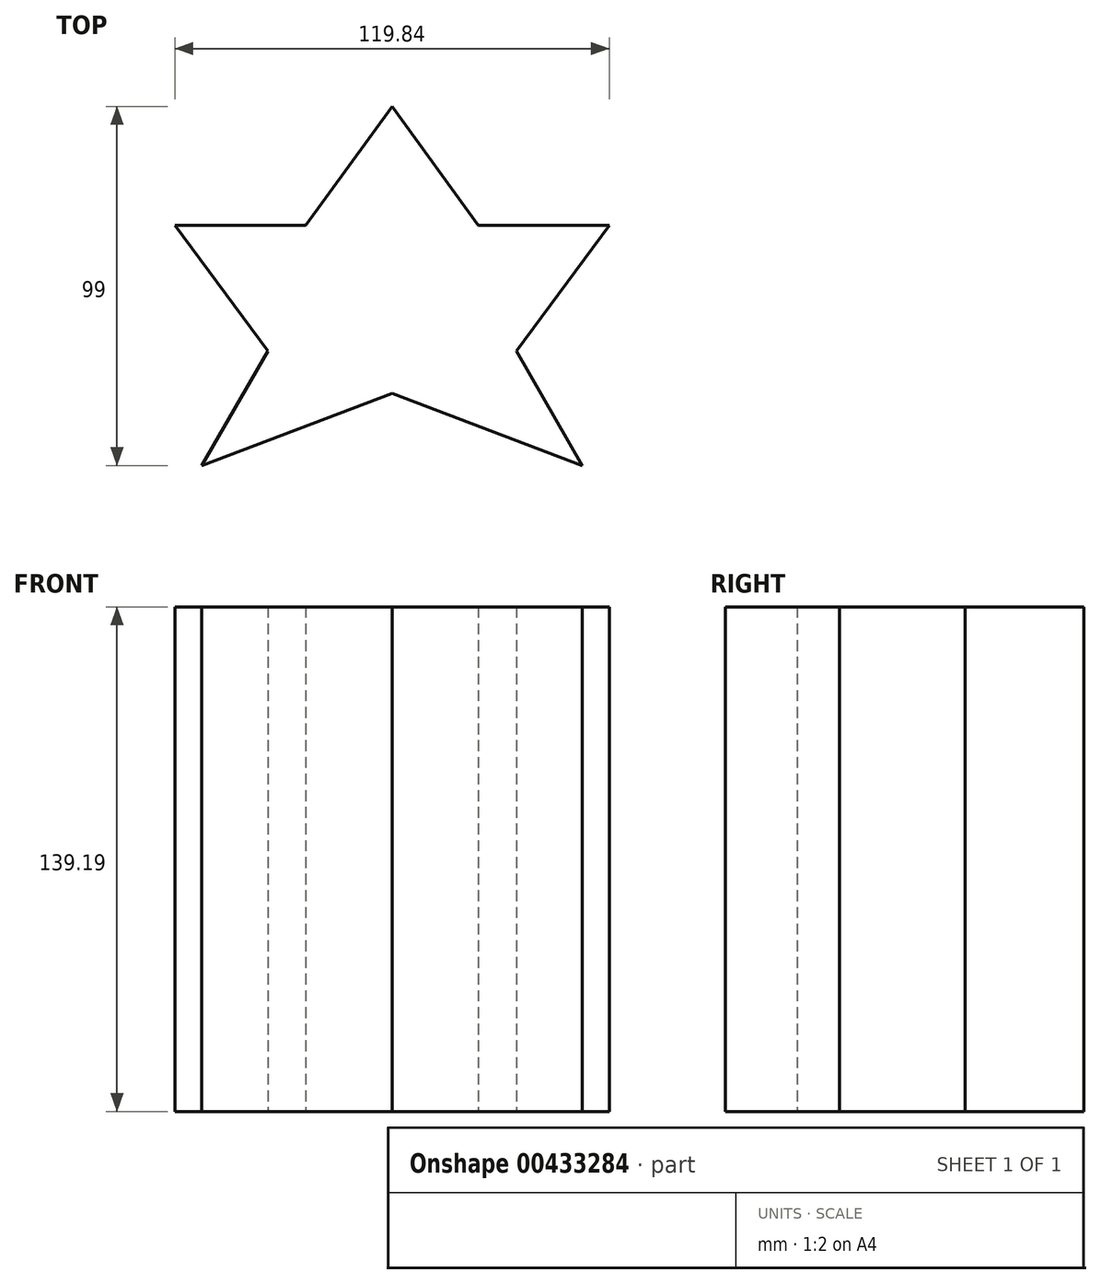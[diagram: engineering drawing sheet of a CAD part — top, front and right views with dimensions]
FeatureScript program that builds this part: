
annotation { "Feature Type Name" : "Feature", "Feature Type Description" : "" }
export const myFeature = defineFeature(function(context is Context, id is Id, definition is map)
    precondition{}
    {
        {
            var Q0;
            Q0=qCreatedBy(makeId("Top.planeOp"),FACE);
            var sketch = newSketch(context, id + "F0", { "sketchPlane" : qUnion([Q0])});
            skLineSegment(sketch, "E0", {"start": v(0, 42.4) * mm, "end": v(-23.78, 9.59) * mm});
            skLineSegment(sketch, "E1", {"start": v(-23.78, 9.59) * mm, "end": v(-59.92, 9.59) * mm});
            skLineSegment(sketch, "E2", {"start": v(-59.92, 9.59) * mm, "end": v(-34.3, -25.07) * mm});
            skLineSegment(sketch, "E3", {"start": v(-34.3, -25.07) * mm, "end": v(-52.54, -56.6) * mm});
            skLineSegment(sketch, "E4", {"start": v(-52.54, -56.6) * mm, "end": v(0, -36.69) * mm});
            skLineSegment(sketch, "E5.MirrorCS", {"start": v(0, 42.4) * mm, "end": v(23.78, 9.59) * mm});
            skLineSegment(sketch, "E6.MirrorCS", {"start": v(23.78, 9.59) * mm, "end": v(59.92, 9.59) * mm});
            skLineSegment(sketch, "E7.MirrorCS", {"start": v(59.92, 9.59) * mm, "end": v(34.3, -25.07) * mm});
            skLineSegment(sketch, "E8.MirrorCS", {"start": v(34.3, -25.07) * mm, "end": v(52.54, -56.6) * mm});
            skLineSegment(sketch, "E9.MirrorCS", {"start": v(52.54, -56.6) * mm, "end": v(0, -36.69) * mm});
            skSolve(sketch);
        }
        {
            var Q0;
            Q0=makeQuery(id+"F0.imprint","IMPRINT",FACE,{"disambiguationData":[TD([[makeQuery(id+"F0.imprint","IMPRINT",EDGE,{"derivedFrom":sQuery(id+"F0.wireOp",EDGE,"E0")}),1.0]])]});
            extrude(context, id + "F1", {"entities" : qUnion([Q0]), "depth" : 139.2 * mm});
        }
        {
            var Q0;
            Q0=makeQuery(id+"F1.opExtrude","CAP_FACE",FACE,{"disambiguationData":[OSD([sQuery(id+"F0.wireOp",EDGE,"E0"),sQuery(id+"F0.wireOp",EDGE,"E1"),sQuery(id+"F0.wireOp",EDGE,"E2"),sQuery(id+"F0.wireOp",EDGE,"E3"),sQuery(id+"F0.wireOp",EDGE,"E4"),sQuery(id+"F0.wireOp",EDGE,"E5.MirrorCS"),sQuery(id+"F0.wireOp",EDGE,"E6.MirrorCS"),sQuery(id+"F0.wireOp",EDGE,"E7.MirrorCS"),sQuery(id+"F0.wireOp",EDGE,"E8.MirrorCS"),sQuery(id+"F0.wireOp",EDGE,"E9.MirrorCS")])],"isStart":true});
            var sketch = newSketch(context, id + "F2", { "sketchPlane" : qUnion([Q0])});
            skCircle(sketch, "E10", {"center": v(0, 6.82) * mm, "radius": 27.77 * mm});
            skSolve(sketch);
        }
        {
            var Q0;
            Q0 = qSketchRegion(id + "F2", true);
            extrude(context, id + "F3", {"entities" : qUnion([Q0]), "operationType" : NewBodyOperationType.ADD, "oppositeDirection" : true, "depth" : 135.89 * mm});
        }
        {
            var Q0;
            Q0=makeQuery(id+"F1.opExtrude","CAP_FACE",FACE,{"disambiguationData":[OSD([sQuery(id+"F0.wireOp",EDGE,"E0"),sQuery(id+"F0.wireOp",EDGE,"E1"),sQuery(id+"F0.wireOp",EDGE,"E2"),sQuery(id+"F0.wireOp",EDGE,"E3"),sQuery(id+"F0.wireOp",EDGE,"E4"),sQuery(id+"F0.wireOp",EDGE,"E5.MirrorCS"),sQuery(id+"F0.wireOp",EDGE,"E6.MirrorCS"),sQuery(id+"F0.wireOp",EDGE,"E7.MirrorCS"),sQuery(id+"F0.wireOp",EDGE,"E8.MirrorCS"),sQuery(id+"F0.wireOp",EDGE,"E9.MirrorCS")])],"isStart":true});
            var sketch = newSketch(context, id + "F4", { "sketchPlane" : qUnion([Q0])});
            skLineSegment(sketch, "E11", {"start": v(0, -28.94) * mm, "end": v(-13.64, -6.45) * mm});
            skLineSegment(sketch, "E12", {"start": v(-13.64, -6.45) * mm, "end": v(-49.78, -6.45) * mm});
            skLineSegment(sketch, "E13", {"start": v(-49.78, -6.45) * mm, "end": v(-27.84, 18.62) * mm});
            skLineSegment(sketch, "E14", {"start": v(-27.84, 18.62) * mm, "end": v(-41.66, 49.4) * mm});
            skLineSegment(sketch, "E15", {"start": v(-41.66, 49.4) * mm, "end": v(-4.8, 31.16) * mm});
            skLineSegment(sketch, "E16", {"start": v(-4.8, 31.16) * mm, "end": v(43.7, 48.3) * mm});
            skLineSegment(sketch, "E17", {"start": v(43.7, 48.3) * mm, "end": v(28.57, 29.13) * mm});
            skLineSegment(sketch, "E18", {"start": v(28.57, 29.13) * mm, "end": v(50.7, -4.42) * mm});
            skLineSegment(sketch, "E19", {"start": v(50.7, -4.42) * mm, "end": v(18.07, -6.45) * mm});
            skLineSegment(sketch, "E20", {"start": v(18.07, -6.45) * mm, "end": v(0, -28.94) * mm});
            skSolve(sketch);
        }
        {
            var Q0;
            Q0 = qSketchRegion(id + "F4", true);
            extrude(context, id + "F5", {"entities" : qUnion([Q0]), "operationType" : NewBodyOperationType.ADD, "oppositeDirection" : true, "depth" : 120.14 * mm});
        }
    });
